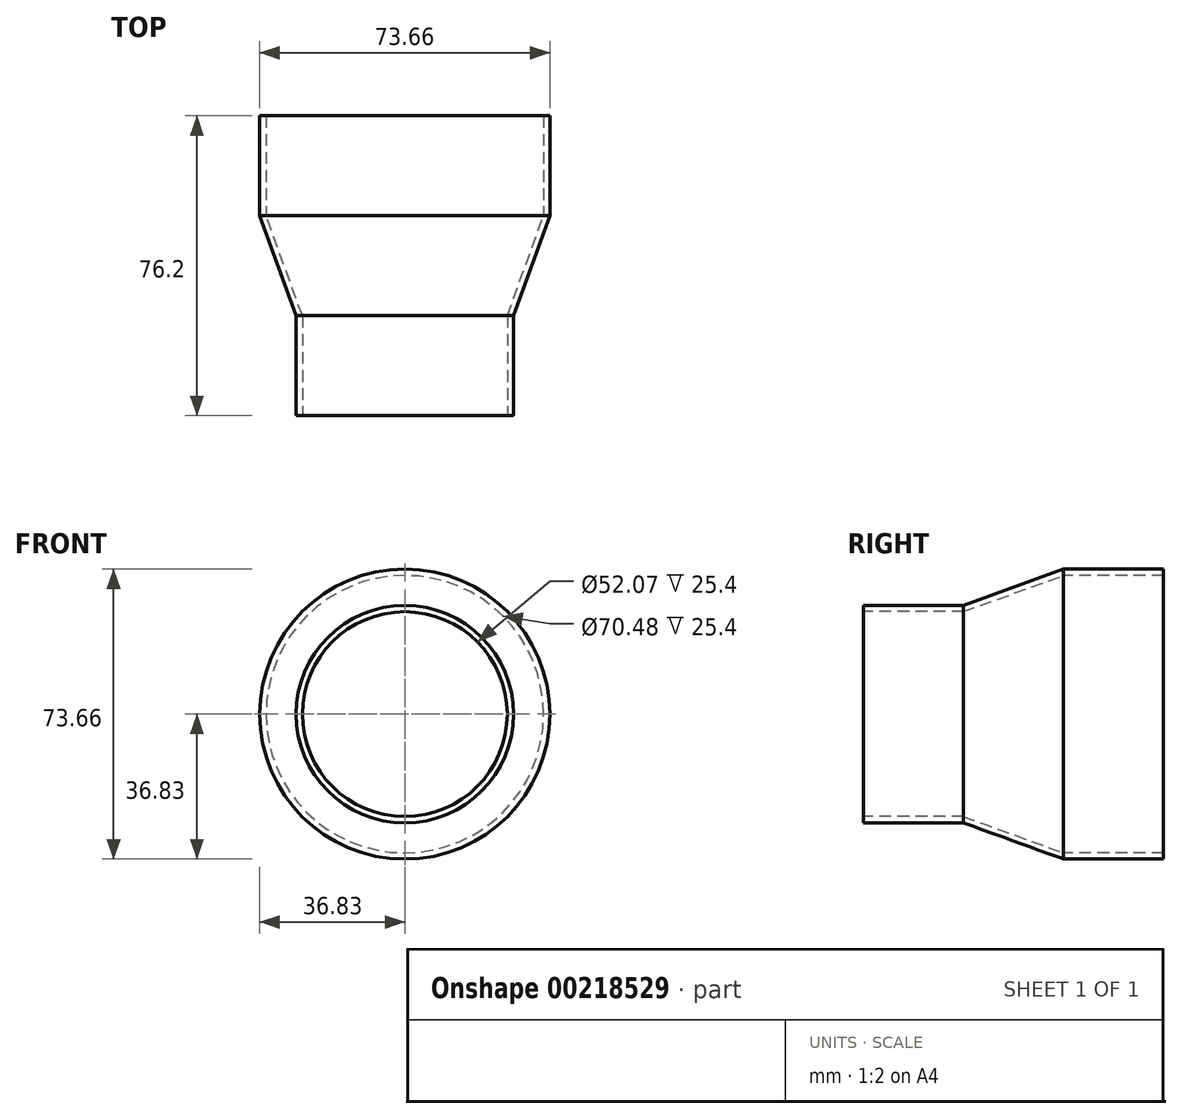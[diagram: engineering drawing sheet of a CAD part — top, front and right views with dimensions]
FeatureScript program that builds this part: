
annotation { "Feature Type Name" : "Feature", "Feature Type Description" : "" }
export const myFeature = defineFeature(function(context is Context, id is Id, definition is map)
    precondition{}
    {
        {
            var Q0;
            Q0=qCreatedBy(makeId("Right.planeOp"),FACE);
            var sketch = newSketch(context, id + "F0", { "sketchPlane" : qUnion([Q0])});
            skPoint(sketch, "E0", {"position": v(-25.4, 64.13) * mm});
            skPoint(sketch, "E1", {"position": v(-25.4, 65.72) * mm});
            skPoint(sketch, "E2", {"position": v(0, 65.72) * mm});
            skPoint(sketch, "E3", {"position": v(0, 64.13) * mm});
            skPoint(sketch, "E4", {"position": v(25.4, 73.34) * mm});
            skPoint(sketch, "E5", {"position": v(25.4, 74.93) * mm});
            skLineSegment(sketch, "E6", {"start": v(-25.4, 65.72) * mm, "end": v(-25.4, 64.13) * mm});
            skLineSegment(sketch, "E7", {"start": v(0, 64.13) * mm, "end": v(25.4, 73.34) * mm});
            skLineSegment(sketch, "E8", {"start": v(25.4, 74.93) * mm, "end": v(0, 65.72) * mm});
            skLineSegment(sketch, "E9", {"start": v(-25.4, 65.72) * mm, "end": v(0, 65.72) * mm});
            skLineSegment(sketch, "E10", {"start": v(25.4, 74.93) * mm, "end": v(25.4, 73.34) * mm});
            skLineSegment(sketch, "E11", {"start": v(-25.4, 64.13) * mm, "end": v(0, 64.13) * mm});
            skPoint(sketch, "E12", {"position": v(0, 38.1) * mm});
            skLineSegment(sketch, "E13", {"start": v(-25.4, 38.1) * mm, "end": v(71.09, 38.1) * mm});
            skSolve(sketch);
        }
        {
            var Q0;
            Q0 = qSketchRegion(id + "F0", true);
            var Q1;
            Q1=sQuery(id+"F0.wireOp",EDGE,"E13");
            revolve(context, id + "F1", {"entities" : qUnion([Q0]), "axis" : qUnion([Q1]), "revolveType" : RevolveType.FULL});
        }
        {
            var Q0;
            Q0=makeQuery(id+"F1.opRevolve","SWEPT_FACE",FACE,{"disambiguationData":[OSD([sQuery(id+"F0.wireOp",EDGE,"E10")])]});
            extrude(context, id + "F2", {"entities" : qUnion([Q0]), "operationType" : NewBodyOperationType.ADD, "depth" : 25.4 * mm});
        }
    });
